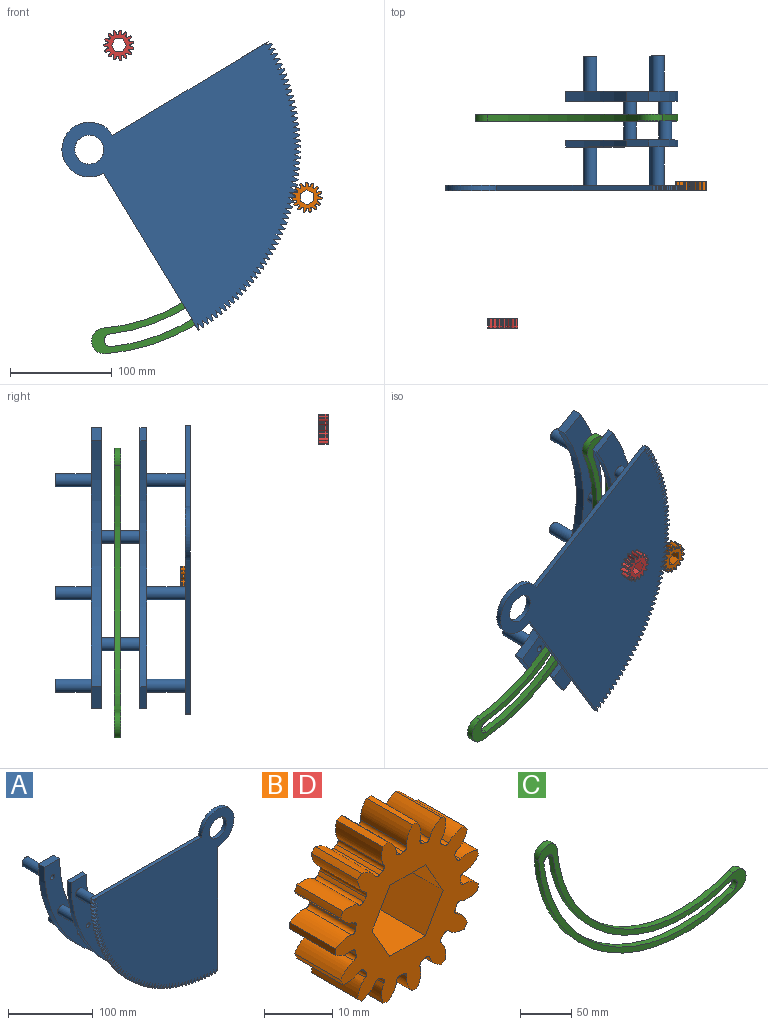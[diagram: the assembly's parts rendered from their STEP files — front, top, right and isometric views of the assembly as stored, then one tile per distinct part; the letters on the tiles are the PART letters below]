
ASSEMBLY  parts=4 mates=2
PART A: 217 faces, bbox 234.6x132.6x234.5 mm
  f0: extruded ~5.08x4.11mm, area 22mm2, adj f1,f2,f178,f180
  f1: plane 234.57x234.55mm, normal (0,-1,0), area 34241.1mm2, adj f0,f3,f4,f5,f6,f7,f8,f9
  f2: plane 234.57x234.55mm, normal (0,1,0), area 33861.1mm2, adj f0,f3,f4,f5,f6,f7,f8,f9
  f3: cylinder r=207.58mm len=5.08mm, axis (0,1,0), area 3.6mm2, adj f1,f2,f4,f179
  f4: extruded ~5.89x5.08mm, area 31.6mm2, adj f1,f2,f3,f5
  f5: extruded ~5.83x5.08mm, area 31.6mm2, adj f1,f2,f4,f6
  f6: cylinder r=207.58mm len=5.08mm, axis (0,1,0), area 7.3mm2, adj f1,f2,f5,f7
  f7: extruded ~5.94x5.08mm, area 31.6mm2, adj f1,f2,f6,f8
  f8: extruded ~5.77x5.08mm, area 31.6mm2, adj f1,f2,f7,f9
  f9: cylinder r=207.58mm len=5.08mm, axis (0,1,0), area 7.3mm2, adj f1,f2,f8,f10
  f10: extruded ~5.98x5.08mm, area 31.6mm2, adj f1,f2,f9,f11
  f11: extruded ~5.71x5.08mm, area 31.6mm2, adj f1,f2,f10,f12
  f12: cylinder r=207.58mm len=5.08mm, axis (0,1,0), area 7.3mm2, adj f1,f2,f11,f13
  f13: extruded ~6.02x5.08mm, area 31.6mm2, adj f1,f2,f12,f14
  f14: extruded ~5.64x5.08mm, area 31.6mm2, adj f1,f2,f13,f15
  f15: cylinder r=207.58mm len=5.08mm, axis (0,1,0), area 7.3mm2, adj f1,f2,f14,f16
  f16: extruded ~6.06x5.08mm, area 31.6mm2, adj f1,f2,f15,f17
  f17: extruded ~5.57x5.08mm, area 31.6mm2, adj f1,f2,f16,f18
  f18: cylinder r=207.58mm len=5.08mm, axis (0,1,0), area 7.3mm2, adj f1,f2,f17,f19
  f19: extruded ~6.1x5.08mm, area 31.6mm2, adj f1,f2,f18,f20
  f20: extruded ~5.49x5.08mm, area 31.6mm2, adj f1,f2,f19,f21
  f21: cylinder r=207.58mm len=5.08mm, axis (0,1,0), area 7.3mm2, adj f1,f2,f20,f22
  f22: extruded ~6.13x5.08mm, area 31.6mm2, adj f1,f2,f21,f23
  f23: extruded ~5.41x5.08mm, area 31.6mm2, adj f1,f2,f22,f24
  f24: cylinder r=207.58mm len=5.08mm, axis (0,1,0), area 7.3mm2, adj f1,f2,f23,f25
  f25: extruded ~6.15x5.08mm, area 31.6mm2, adj f1,f2,f24,f26
  f26: extruded ~5.33x5.08mm, area 31.6mm2, adj f1,f2,f25,f27
  f27: cylinder r=207.58mm len=5.08mm, axis (0,1,0), area 7.3mm2, adj f1,f2,f26,f28
  f28: extruded ~6.17x5.08mm, area 31.6mm2, adj f1,f2,f27,f29
  f29: extruded ~5.24x5.08mm, area 31.6mm2, adj f1,f2,f28,f30
  f30: cylinder r=207.58mm len=5.08mm, axis (0,1,0), area 7.3mm2, adj f1,f2,f29,f31
  f31: extruded ~6.19x5.08mm, area 31.6mm2, adj f1,f2,f30,f32
  f32: extruded ~5.15x5.08mm, area 31.6mm2, adj f1,f2,f31,f33
  f33: cylinder r=207.58mm len=5.08mm, axis (0,1,0), area 7.3mm2, adj f1,f2,f32,f34
  f34: extruded ~6.2x5.08mm, area 31.6mm2, adj f1,f2,f33,f35
  f35: extruded ~5.08x5.06mm, area 31.6mm2, adj f1,f2,f34,f36
  f36: cylinder r=207.58mm len=5.08mm, axis (0,1,0), area 7.3mm2, adj f1,f2,f35,f37
  f37: extruded ~6.21x5.08mm, area 31.6mm2, adj f1,f2,f36,f38
  f38: extruded ~5.08x4.96mm, area 31.6mm2, adj f1,f2,f37,f39
  f39: cylinder r=207.58mm len=5.08mm, axis (0,1,0), area 7.3mm2, adj f1,f2,f38,f40
  f40: extruded ~6.21x5.08mm, area 31.6mm2, adj f1,f2,f39,f41
  f41: extruded ~5.08x4.86mm, area 31.6mm2, adj f1,f2,f40,f42
  f42: cylinder r=207.58mm len=5.08mm, axis (0,1,0), area 7.3mm2, adj f1,f2,f41,f43
  f43: extruded ~6.21x5.08mm, area 31.6mm2, adj f1,f2,f42,f44
  f44: extruded ~5.08x4.75mm, area 31.6mm2, adj f1,f2,f43,f45
  f45: cylinder r=207.58mm len=5.08mm, axis (0,1,0), area 7.3mm2, adj f1,f2,f44,f46
  f46: extruded ~6.2x5.08mm, area 31.6mm2, adj f1,f2,f45,f47
  f47: extruded ~5.08x4.65mm, area 31.6mm2, adj f1,f2,f46,f48
  f48: cylinder r=207.58mm len=5.08mm, axis (0,1,0), area 7.3mm2, adj f1,f2,f47,f49
  f49: extruded ~6.19x5.08mm, area 31.6mm2, adj f1,f2,f48,f50
  f50: extruded ~5.08x4.53mm, area 31.6mm2, adj f1,f2,f49,f51
  f51: cylinder r=207.58mm len=5.08mm, axis (0,1,0), area 7.3mm2, adj f1,f2,f50,f52
  f52: extruded ~6.18x5.08mm, area 31.6mm2, adj f1,f2,f51,f53
  f53: extruded ~5.08x4.42mm, area 31.6mm2, adj f1,f2,f52,f54
  f54: cylinder r=207.58mm len=5.08mm, axis (0,1,0), area 7.3mm2, adj f1,f2,f53,f55
  f55: extruded ~6.16x5.08mm, area 31.6mm2, adj f1,f2,f54,f56
  f56: extruded ~5.08x4.48mm, area 31.6mm2, adj f1,f2,f55,f57
  f57: cylinder r=207.58mm len=5.08mm, axis (0,1,0), area 7.3mm2, adj f1,f2,f56,f58
  f58: extruded ~6.13x5.08mm, area 31.6mm2, adj f1,f2,f57,f59
  f59: extruded ~5.08x4.59mm, area 31.6mm2, adj f1,f2,f58,f60
  f60: cylinder r=207.58mm len=5.08mm, axis (0,1,0), area 7.3mm2, adj f1,f2,f59,f61
  f61: extruded ~6.11x5.08mm, area 31.6mm2, adj f1,f2,f60,f62
  f62: extruded ~5.08x4.7mm, area 31.6mm2, adj f1,f2,f61,f63
  f63: cylinder r=207.58mm len=5.08mm, axis (0,1,0), area 7.3mm2, adj f1,f2,f62,f64
  f64: extruded ~6.07x5.08mm, area 31.6mm2, adj f1,f2,f63,f65
  f65: extruded ~5.08x4.81mm, area 31.6mm2, adj f1,f2,f64,f66
  f66: cylinder r=207.58mm len=5.08mm, axis (0,1,0), area 7.3mm2, adj f1,f2,f65,f67
  f67: extruded ~6.04x5.08mm, area 31.6mm2, adj f1,f2,f66,f68
  f68: extruded ~5.08x4.91mm, area 31.6mm2, adj f1,f2,f67,f69
  f69: cylinder r=207.58mm len=5.08mm, axis (0,1,0), area 7.3mm2, adj f1,f2,f68,f70
  f70: extruded ~5.99x5.08mm, area 31.6mm2, adj f1,f2,f69,f71
  f71: extruded ~5.08x5.01mm, area 31.6mm2, adj f1,f2,f70,f72
  f72: cylinder r=207.58mm len=5.08mm, axis (0,1,0), area 7.3mm2, adj f1,f2,f71,f73
  f73: extruded ~5.95x5.08mm, area 31.6mm2, adj f1,f2,f72,f74
  f74: extruded ~5.11x5.08mm, area 31.6mm2, adj f1,f2,f73,f75
  f75: cylinder r=207.58mm len=5.08mm, axis (0,1,0), area 7.3mm2, adj f1,f2,f74,f76
  f76: extruded ~5.9x5.08mm, area 31.6mm2, adj f1,f2,f75,f77
  f77: extruded ~5.2x5.08mm, area 31.6mm2, adj f1,f2,f76,f78
  f78: cylinder r=207.58mm len=5.08mm, axis (0,1,0), area 7.3mm2, adj f1,f2,f77,f79
  f79: extruded ~5.85x5.08mm, area 31.6mm2, adj f1,f2,f78,f80
  f80: extruded ~5.29x5.08mm, area 31.6mm2, adj f1,f2,f79,f81
  f81: cylinder r=207.58mm len=5.08mm, axis (0,1,0), area 7.3mm2, adj f1,f2,f80,f82
  f82: extruded ~5.79x5.08mm, area 31.6mm2, adj f1,f2,f81,f83
  f83: extruded ~5.38x5.08mm, area 31.6mm2, adj f1,f2,f82,f84
  f84: cylinder r=207.58mm len=5.08mm, axis (0,1,0), area 7.3mm2, adj f1,f2,f83,f85
  f85: extruded ~5.73x5.08mm, area 31.6mm2, adj f1,f2,f84,f86
  f86: extruded ~5.46x5.08mm, area 31.6mm2, adj f1,f2,f85,f87
  f87: cylinder r=207.58mm len=5.08mm, axis (0,1,0), area 7.3mm2, adj f1,f2,f86,f88
  f88: extruded ~5.66x5.08mm, area 31.6mm2, adj f1,f2,f87,f89
  f89: extruded ~5.53x5.08mm, area 31.6mm2, adj f1,f2,f88,f90
  f90: cylinder r=207.58mm len=5.08mm, axis (0,1,0), area 7.3mm2, adj f1,f2,f89,f91
  f91: extruded ~5.59x5.08mm, area 31.6mm2, adj f1,f2,f90,f92
  f92: extruded ~5.61x5.08mm, area 31.6mm2, adj f1,f2,f91,f93
  f93: cylinder r=207.58mm len=5.08mm, axis (0,1,0), area 7.3mm2, adj f1,f2,f92,f94
  f94: extruded ~5.51x5.08mm, area 31.6mm2, adj f1,f2,f93,f95
  f95: extruded ~5.68x5.08mm, area 31.6mm2, adj f1,f2,f94,f96
  f96: cylinder r=207.58mm len=5.08mm, axis (0,1,0), area 7.3mm2, adj f1,f2,f95,f97
  f97: extruded ~5.44x5.08mm, area 31.6mm2, adj f1,f2,f96,f98
  f98: extruded ~5.74x5.08mm, area 31.6mm2, adj f1,f2,f97,f99
  f99: cylinder r=207.58mm len=5.08mm, axis (0,1,0), area 7.3mm2, adj f1,f2,f98,f100
  f100: extruded ~5.35x5.08mm, area 31.6mm2, adj f1,f2,f99,f101
  f101: extruded ~5.8x5.08mm, area 31.6mm2, adj f1,f2,f100,f102
  f102: cylinder r=207.58mm len=5.08mm, axis (0,1,0), area 7.3mm2, adj f1,f2,f101,f103
  f103: extruded ~5.27x5.08mm, area 31.6mm2, adj f1,f2,f102,f104
  f104: extruded ~5.86x5.08mm, area 31.6mm2, adj f1,f2,f103,f105
  f105: cylinder r=207.58mm len=5.08mm, axis (0,1,0), area 7.3mm2, adj f1,f2,f104,f106
  f106: extruded ~5.18x5.08mm, area 31.6mm2, adj f1,f2,f105,f107
  f107: extruded ~5.91x5.08mm, area 31.6mm2, adj f1,f2,f106,f108
  f108: cylinder r=207.58mm len=5.08mm, axis (0,1,0), area 7.3mm2, adj f1,f2,f107,f109
  f109: extruded ~5.09x5.08mm, area 31.6mm2, adj f1,f2,f108,f110
  f110: extruded ~5.96x5.08mm, area 31.6mm2, adj f1,f2,f109,f111
  f111: cylinder r=207.58mm len=5.08mm, axis (0,1,0), area 7.3mm2, adj f1,f2,f110,f112
  f112: extruded ~5.08x4.99mm, area 31.6mm2, adj f1,f2,f111,f113
  f113: extruded ~6.01x5.08mm, area 31.6mm2, adj f1,f2,f112,f114
  f114: cylinder r=207.58mm len=5.08mm, axis (0,1,0), area 7.3mm2, adj f1,f2,f113,f115
  f115: extruded ~5.08x4.89mm, area 31.6mm2, adj f1,f2,f114,f116
  f116: extruded ~6.05x5.08mm, area 31.6mm2, adj f1,f2,f115,f117
  f117: cylinder r=207.58mm len=5.08mm, axis (0,1,0), area 7.3mm2, adj f1,f2,f116,f118
  f118: extruded ~5.08x4.78mm, area 31.6mm2, adj f1,f2,f117,f119
  f119: extruded ~6.08x5.08mm, area 31.6mm2, adj f1,f2,f118,f120
  f120: cylinder r=207.58mm len=5.08mm, axis (0,1,0), area 7.3mm2, adj f1,f2,f119,f121
  f121: extruded ~5.08x4.68mm, area 31.6mm2, adj f1,f2,f120,f122
  f122: extruded ~6.11x5.08mm, area 31.6mm2, adj f1,f2,f121,f123
  f123: cylinder r=207.58mm len=5.08mm, axis (0,1,0), area 7.3mm2, adj f1,f2,f122,f124
  f124: extruded ~5.08x4.56mm, area 31.6mm2, adj f1,f2,f123,f125
  f125: extruded ~6.14x5.08mm, area 31.6mm2, adj f1,f2,f124,f126
  f126: cylinder r=207.58mm len=5.08mm, axis (0,1,0), area 7.3mm2, adj f1,f2,f125,f127
  f127: extruded ~5.08x4.45mm, area 31.6mm2, adj f1,f2,f126,f128
  f128: extruded ~6.16x5.08mm, area 31.6mm2, adj f1,f2,f127,f129
  f129: cylinder r=207.58mm len=5.08mm, axis (0,1,0), area 7.3mm2, adj f1,f2,f128,f130
  f130: extruded ~5.08x4.45mm, area 31.6mm2, adj f1,f2,f129,f131
  f131: extruded ~6.18x5.08mm, area 31.6mm2, adj f1,f2,f130,f132
  f132: cylinder r=207.58mm len=5.08mm, axis (0,1,0), area 7.3mm2, adj f1,f2,f131,f133
  f133: extruded ~5.08x4.56mm, area 31.6mm2, adj f1,f2,f132,f134
  f134: extruded ~6.19x5.08mm, area 31.6mm2, adj f1,f2,f133,f135
  f135: cylinder r=207.58mm len=5.08mm, axis (0,1,0), area 7.3mm2, adj f1,f2,f134,f136
  f136: extruded ~5.08x4.67mm, area 31.6mm2, adj f1,f2,f135,f137
  f137: extruded ~6.2x5.08mm, area 31.6mm2, adj f1,f2,f136,f138
  f138: cylinder r=207.58mm len=5.08mm, axis (0,1,0), area 7.3mm2, adj f1,f2,f137,f139
  f139: extruded ~5.08x4.78mm, area 31.6mm2, adj f1,f2,f138,f140
  f140: extruded ~6.21x5.08mm, area 31.6mm2, adj f1,f2,f139,f141
  f141: cylinder r=207.58mm len=5.08mm, axis (0,1,0), area 7.3mm2, adj f1,f2,f140,f142
  f142: extruded ~5.08x4.88mm, area 31.6mm2, adj f1,f2,f141,f143
  f143: extruded ~6.21x5.08mm, area 31.6mm2, adj f1,f2,f142,f144
  f144: cylinder r=207.58mm len=5.08mm, axis (0,1,0), area 7.3mm2, adj f1,f2,f143,f145
  f145: extruded ~5.08x4.99mm, area 31.6mm2, adj f1,f2,f144,f146
  f146: extruded ~6.21x5.08mm, area 31.6mm2, adj f1,f2,f145,f147
  f147: cylinder r=207.58mm len=5.08mm, axis (0,1,0), area 7.3mm2, adj f1,f2,f146,f148
  f148: extruded ~5.08x5.08mm, area 31.6mm2, adj f1,f2,f147,f149
  f149: extruded ~6.2x5.08mm, area 31.6mm2, adj f1,f2,f148,f150
  f150: cylinder r=207.58mm len=5.08mm, axis (0,1,0), area 7.3mm2, adj f1,f2,f149,f151
  f151: extruded ~5.18x5.08mm, area 31.6mm2, adj f1,f2,f150,f152
  f152: extruded ~6.18x5.08mm, area 31.6mm2, adj f1,f2,f151,f153
  f153: cylinder r=207.58mm len=5.08mm, axis (0,1,0), area 7.3mm2, adj f1,f2,f152,f154
  f154: extruded ~5.27x5.08mm, area 31.6mm2, adj f1,f2,f153,f155
  f155: extruded ~6.17x5.08mm, area 31.6mm2, adj f1,f2,f154,f156
  f156: cylinder r=207.58mm len=5.08mm, axis (0,1,0), area 7.3mm2, adj f1,f2,f155,f157
  f157: extruded ~5.35x5.08mm, area 31.6mm2, adj f1,f2,f156,f158
  f158: extruded ~6.14x5.08mm, area 31.6mm2, adj f1,f2,f157,f159
  f159: cylinder r=207.58mm len=5.08mm, axis (0,1,0), area 7.3mm2, adj f1,f2,f158,f160
  f160: extruded ~5.43x5.08mm, area 31.6mm2, adj f1,f2,f159,f161
  f161: extruded ~6.12x5.08mm, area 31.6mm2, adj f1,f2,f160,f162
  f162: cylinder r=207.58mm len=5.08mm, axis (0,1,0), area 7.3mm2, adj f1,f2,f161,f163
  f163: extruded ~5.51x5.08mm, area 31.6mm2, adj f1,f2,f162,f164
  f164: extruded ~6.09x5.08mm, area 31.6mm2, adj f1,f2,f163,f165
  f165: cylinder r=207.58mm len=5.08mm, axis (0,1,0), area 7.3mm2, adj f1,f2,f164,f166
  f166: extruded ~5.59x5.08mm, area 31.6mm2, adj f1,f2,f165,f167
  f167: extruded ~6.05x5.08mm, area 31.6mm2, adj f1,f2,f166,f168
  f168: cylinder r=207.58mm len=5.08mm, axis (0,1,0), area 7.3mm2, adj f1,f2,f167,f169
  f169: extruded ~5.66x5.08mm, area 31.6mm2, adj f1,f2,f168,f170
  f170: extruded ~6.01x5.08mm, area 31.6mm2, adj f1,f2,f169,f171
  f171: cylinder r=207.58mm len=5.08mm, axis (0,1,0), area 7.3mm2, adj f1,f2,f170,f172
  f172: extruded ~5.72x5.08mm, area 31.6mm2, adj f1,f2,f171,f173
  f173: extruded ~5.97x5.08mm, area 31.6mm2, adj f1,f2,f172,f174
  f174: cylinder r=207.58mm len=5.08mm, axis (0,1,0), area 7.3mm2, adj f1,f2,f173,f175
  f175: extruded ~5.79x5.08mm, area 31.6mm2, adj f1,f2,f174,f176
  f176: extruded ~5.92x5.08mm, area 31.6mm2, adj f1,f2,f175,f177
  f177: cylinder r=207.58mm len=5.08mm, axis (0,1,0), area 7.3mm2, adj f1,f2,f176,f178
  f178: extruded ~5.84x5.08mm, area 31.6mm2, adj f0,f1,f2,f177
  f179: plane 180.59x5.08mm, normal (0,0,1), area 917.4mm2, adj f1,f2,f3,f181
  f180: plane 178.83x5.08mm, normal (1,0,0), area 908.4mm2, adj f0,f1,f2,f181
  f181: cylinder r=26.99mm len=53.98mm, axis (0,1,0), area 646.1mm2, adj f1,f2,f179,f180
  f182: cylinder r=14.29mm len=28.58mm, axis (0,1,0), area 456mm2, adj f1,f2
  f183: cylinder r=6.35mm len=38.1mm, axis (0,-1,0), area 1520.1mm2, adj f2,f193
  f184: cylinder r=6.35mm len=38.1mm, axis (0,-1,0), area 1520.1mm2, adj f2,f193
  f185: cylinder r=6.35mm len=38.1mm, axis (0,-1,0), area 1520.1mm2, adj f2,f193
  f186: plane 25.4x6.6mm, normal (1,0,0), area 167.7mm2, adj f187,f190,f192,f193
  f187: cylinder r=201.61mm len=201.61mm, axis (0,-1,0), area 2091.4mm2, adj f186,f188,f192,f193
  f188: plane 25.4x6.6mm, normal (0,0,1), area 167.7mm2, adj f187,f190,f192,f193
  f189: cylinder r=3.17mm len=54.61mm, axis (0,-1,0), area 1089.4mm2, adj f193,f216
  f190: cylinder r=176.21mm len=176.21mm, axis (0,-1,0), area 1827.9mm2, adj f186,f188,f192,f193
  f191: cylinder r=3.17mm len=54.61mm, axis (0,-1,0), area 1089.4mm2, adj f193,f216
  f192: plane 201.61x201.61mm, normal (0,1,0), area 7188.9mm2, adj f186,f187,f188,f190,f195,f197,f199,f200
  f193: plane 201.61x201.61mm, normal (0,-1,0), area 7093.9mm2, adj f183,f184,f185,f186,f187,f188,f189,f190
  f194: plane 6.35x6.35mm, normal (0,1,0), area 31.7mm2, adj f195
  f195: cylinder r=3.17mm len=44.7mm, axis (0,-1,0), area 891.8mm2, adj f192,f194
  f196: plane 6.35x6.35mm, normal (0,1,0), area 31.7mm2, adj f197
  f197: cylinder r=3.17mm len=44.7mm, axis (0,-1,0), area 891.8mm2, adj f192,f196
  f198: plane 6.35x6.35mm, normal (0,1,0), area 31.7mm2, adj f199
  f199: cylinder r=3.17mm len=44.7mm, axis (0,-1,0), area 891.8mm2, adj f192,f198
  f200: cylinder r=6.35mm len=38.1mm, axis (0,-1,0), area 1520.1mm2, adj f192,f209
  f201: cylinder r=6.35mm len=38.1mm, axis (0,-1,0), area 1520.1mm2, adj f192,f209
  f202: plane 25.4x9.91mm, normal (0,0,1), area 251.6mm2, adj f203,f205,f209,f216
  f203: cylinder r=176.21mm len=176.21mm, axis (0,-1,0), area 2741.9mm2, adj f202,f204,f209,f216
  f204: plane 25.4x9.91mm, normal (1,0,0), area 251.6mm2, adj f203,f205,f209,f216
  f205: cylinder r=201.61mm len=201.61mm, axis (0,-1,0), area 3137.2mm2, adj f202,f204,f209,f216
  f206: cylinder r=3.17mm len=44.7mm, axis (0,-1,0), area 891.8mm2, adj f209,f215
  f207: cylinder r=3.17mm len=44.7mm, axis (0,-1,0), area 891.8mm2, adj f209,f213
  f208: cylinder r=3.17mm len=44.7mm, axis (0,-1,0), area 891.8mm2, adj f209,f211
  f209: plane 201.61x201.61mm, normal (0,-1,0), area 7188.9mm2, adj f200,f201,f202,f203,f204,f205,f206,f207
  f210: cylinder r=6.35mm len=34.8mm, axis (0,-1,0), area 1388.4mm2, adj f211,f216
  f211: plane 12.7x12.7mm, normal (0,1,0), area 95mm2, adj f208,f210
  f212: cylinder r=6.35mm len=34.8mm, axis (0,-1,0), area 1388.4mm2, adj f213,f216
  f213: plane 12.7x12.7mm, normal (0,1,0), area 95mm2, adj f207,f212
  f214: cylinder r=6.35mm len=34.8mm, axis (0,-1,0), area 1388.4mm2, adj f215,f216
  f215: plane 12.7x12.7mm, normal (0,1,0), area 95mm2, adj f206,f214
  f216: plane 201.61x201.61mm, normal (0,1,0), area 7093.9mm2, adj f189,f191,f202,f203,f204,f205,f210,f212
PART B: 98 faces, bbox 29.6x9.5x29.8 mm
  f0: plane 29.76x29.6mm, normal (0,-1,0), area 386.4mm2, adj f2,f3,f4,f5,f6,f7,f8,f9
  f1: plane 29.76x29.6mm, normal (0,1,0), area 386.4mm2, adj f2,f3,f4,f5,f6,f7,f8,f9
  f2: extruded ~9.53x3.13mm, area 34mm2, adj f0,f1,f61,f62
  f3: cylinder r=10.95mm len=9.53mm, axis (0,1,0), area 6.9mm2, adj f0,f1,f62,f63
  f4: extruded ~9.53x3.13mm, area 34mm2, adj f0,f1,f5,f63
  f5: cylinder r=14.89mm len=9.53mm, axis (0,1,0), area 10.9mm2, adj f0,f1,f4,f6
  f6: extruded ~9.53x3.47mm, area 34mm2, adj f0,f1,f5,f64
  f7: cylinder r=10.95mm len=9.53mm, axis (0,1,0), area 6.9mm2, adj f0,f1,f64,f65
  f8: extruded ~9.53x2.64mm, area 34mm2, adj f0,f1,f9,f65
  f9: cylinder r=14.89mm len=9.53mm, axis (0,1,0), area 10.9mm2, adj f0,f1,f8,f10
  f10: extruded ~9.53x3.21mm, area 34mm2, adj f0,f1,f9,f66
  f11: cylinder r=10.95mm len=9.53mm, axis (0,1,0), area 6.9mm2, adj f0,f1,f66,f67
  f12: extruded ~9.53x3.33mm, area 34mm2, adj f0,f1,f13,f67
  f13: cylinder r=14.89mm len=9.53mm, axis (0,1,0), area 10.9mm2, adj f0,f1,f12,f14
  f14: extruded ~9.53x2.52mm, area 34mm2, adj f0,f1,f13,f68
  f15: cylinder r=10.95mm len=9.53mm, axis (0,1,0), area 6.9mm2, adj f0,f1,f68,f69
  f16: extruded ~9.53x3.44mm, area 34mm2, adj f0,f1,f17,f69
  f17: cylinder r=14.89mm len=9.53mm, axis (0,1,0), area 10.9mm2, adj f0,f1,f16,f18
  f18: extruded ~9.53x3.27mm, area 34mm2, adj f0,f1,f17,f70
  f19: cylinder r=10.95mm len=9.53mm, axis (0,1,0), area 6.9mm2, adj f0,f1,f70,f71
  f20: extruded ~9.53x2.96mm, area 34mm2, adj f0,f1,f21,f71
  f21: cylinder r=14.89mm len=9.53mm, axis (0,1,0), area 10.9mm2, adj f0,f1,f20,f22
  f22: extruded ~9.53x3.46mm, area 34mm2, adj f0,f1,f21,f72
  f23: cylinder r=10.95mm len=9.53mm, axis (0,1,0), area 6.9mm2, adj f0,f1,f72,f73
  f24: extruded ~9.53x2.86mm, area 34mm2, adj f0,f1,f25,f73
  f25: cylinder r=14.89mm len=9.53mm, axis (0,1,0), area 10.9mm2, adj f0,f1,f24,f26
  f26: extruded ~9.53x3.05mm, area 34mm2, adj f0,f1,f25,f74
  f27: cylinder r=10.95mm len=9.53mm, axis (0,1,0), area 6.9mm2, adj f0,f1,f74,f75
  f28: extruded ~9.53x3.41mm, area 34mm2, adj f0,f1,f29,f75
  f29: cylinder r=14.89mm len=9.53mm, axis (0,1,0), area 10.9mm2, adj f0,f1,f28,f30
  f30: extruded ~9.53x2.75mm, area 34mm2, adj f0,f1,f29,f76
  f31: cylinder r=10.95mm len=9.53mm, axis (0,1,0), area 6.9mm2, adj f0,f1,f76,f77
  f32: extruded ~9.53x3.38mm, area 34mm2, adj f0,f1,f33,f77
  f33: cylinder r=14.89mm len=9.53mm, axis (0,1,0), area 10.9mm2, adj f0,f1,f32,f34
  f34: extruded ~9.53x3.38mm, area 34mm2, adj f0,f1,f33,f78
  f35: cylinder r=10.95mm len=9.53mm, axis (0,1,0), area 6.9mm2, adj f0,f1,f78,f79
  f36: extruded ~9.53x2.75mm, area 34mm2, adj f0,f1,f37,f79
  f37: cylinder r=14.89mm len=9.53mm, axis (0,1,0), area 10.9mm2, adj f0,f1,f36,f38
  f38: extruded ~9.53x3.41mm, area 34mm2, adj f0,f1,f37,f80
  f39: cylinder r=10.95mm len=9.53mm, axis (0,1,0), area 6.9mm2, adj f0,f1,f80,f81
  f40: extruded ~9.53x3.05mm, area 34mm2, adj f0,f1,f41,f81
  f41: cylinder r=14.89mm len=9.53mm, axis (0,1,0), area 10.9mm2, adj f0,f1,f40,f42
  f42: extruded ~9.53x2.86mm, area 34mm2, adj f0,f1,f41,f82
  f43: cylinder r=10.95mm len=9.53mm, axis (0,1,0), area 6.9mm2, adj f0,f1,f82,f83
  f44: extruded ~9.53x3.46mm, area 34mm2, adj f0,f1,f45,f83
  f45: cylinder r=14.89mm len=9.53mm, axis (0,1,0), area 10.9mm2, adj f0,f1,f44,f46
  f46: extruded ~9.53x2.96mm, area 34mm2, adj f0,f1,f45,f84
  f47: cylinder r=10.95mm len=9.53mm, axis (0,1,0), area 6.9mm2, adj f0,f1,f84,f85
  f48: extruded ~9.53x3.27mm, area 34mm2, adj f0,f1,f49,f85
  f49: cylinder r=14.89mm len=9.53mm, axis (0,1,0), area 10.9mm2, adj f0,f1,f48,f50
  f50: extruded ~9.53x3.44mm, area 34mm2, adj f0,f1,f49,f86
  f51: cylinder r=10.95mm len=9.53mm, axis (0,1,0), area 6.9mm2, adj f0,f1,f86,f87
  f52: extruded ~9.53x2.52mm, area 34mm2, adj f0,f1,f53,f87
  f53: cylinder r=14.89mm len=9.53mm, axis (0,1,0), area 10.9mm2, adj f0,f1,f52,f54
  f54: extruded ~9.53x3.33mm, area 34mm2, adj f0,f1,f53,f88
  f55: cylinder r=10.95mm len=9.53mm, axis (0,1,0), area 6.9mm2, adj f0,f1,f88,f89
  f56: extruded ~9.53x3.21mm, area 34mm2, adj f0,f1,f57,f89
  f57: cylinder r=14.89mm len=9.53mm, axis (0,1,0), area 10.9mm2, adj f0,f1,f56,f58
  f58: extruded ~9.53x2.64mm, area 34mm2, adj f0,f1,f57,f90
  f59: cylinder r=10.95mm len=9.53mm, axis (0,1,0), area 6.9mm2, adj f0,f1,f90,f91
  f60: extruded ~9.53x3.47mm, area 34mm2, adj f0,f1,f61,f91
  f61: cylinder r=14.89mm len=9.53mm, axis (0,1,0), area 10.9mm2, adj f0,f1,f2,f60
  f62: cylinder r=0.65mm len=9.53mm, axis (0,1,0), area 9.5mm2, adj f0,f1,f2,f3
  f63: cylinder r=0.65mm len=9.53mm, axis (0,1,0), area 9.5mm2, adj f0,f1,f3,f4
  f64: cylinder r=0.65mm len=9.53mm, axis (0,1,0), area 9.5mm2, adj f0,f1,f6,f7
  f65: cylinder r=0.65mm len=9.53mm, axis (0,1,0), area 9.5mm2, adj f0,f1,f7,f8
  f66: cylinder r=0.65mm len=9.53mm, axis (0,1,0), area 9.5mm2, adj f0,f1,f10,f11
  f67: cylinder r=0.65mm len=9.53mm, axis (0,1,0), area 9.5mm2, adj f0,f1,f11,f12
  f68: cylinder r=0.65mm len=9.53mm, axis (0,1,0), area 9.5mm2, adj f0,f1,f14,f15
  f69: cylinder r=0.65mm len=9.53mm, axis (0,1,0), area 9.5mm2, adj f0,f1,f15,f16
  f70: cylinder r=0.65mm len=9.53mm, axis (0,1,0), area 9.5mm2, adj f0,f1,f18,f19
  f71: cylinder r=0.65mm len=9.53mm, axis (0,1,0), area 9.5mm2, adj f0,f1,f19,f20
  f72: cylinder r=0.65mm len=9.53mm, axis (0,1,0), area 9.5mm2, adj f0,f1,f22,f23
  f73: cylinder r=0.65mm len=9.53mm, axis (0,1,0), area 9.5mm2, adj f0,f1,f23,f24
  f74: cylinder r=0.65mm len=9.53mm, axis (0,1,0), area 9.5mm2, adj f0,f1,f26,f27
  f75: cylinder r=0.65mm len=9.53mm, axis (0,1,0), area 9.5mm2, adj f0,f1,f27,f28
  f76: cylinder r=0.65mm len=9.53mm, axis (0,1,0), area 9.5mm2, adj f0,f1,f30,f31
  f77: cylinder r=0.65mm len=9.53mm, axis (0,1,0), area 9.5mm2, adj f0,f1,f31,f32
  f78: cylinder r=0.65mm len=9.53mm, axis (0,1,0), area 9.5mm2, adj f0,f1,f34,f35
  f79: cylinder r=0.65mm len=9.53mm, axis (0,1,0), area 9.5mm2, adj f0,f1,f35,f36
  f80: cylinder r=0.65mm len=9.53mm, axis (0,1,0), area 9.5mm2, adj f0,f1,f38,f39
  f81: cylinder r=0.65mm len=9.53mm, axis (0,1,0), area 9.5mm2, adj f0,f1,f39,f40
  f82: cylinder r=0.65mm len=9.53mm, axis (0,1,0), area 9.5mm2, adj f0,f1,f42,f43
  f83: cylinder r=0.65mm len=9.53mm, axis (0,1,0), area 9.5mm2, adj f0,f1,f43,f44
  f84: cylinder r=0.65mm len=9.53mm, axis (0,1,0), area 9.5mm2, adj f0,f1,f46,f47
  f85: cylinder r=0.65mm len=9.53mm, axis (0,1,0), area 9.5mm2, adj f0,f1,f47,f48
  f86: cylinder r=0.65mm len=9.53mm, axis (0,1,0), area 9.5mm2, adj f0,f1,f50,f51
  f87: cylinder r=0.65mm len=9.53mm, axis (0,1,0), area 9.5mm2, adj f0,f1,f51,f52
  f88: cylinder r=0.65mm len=9.53mm, axis (0,1,0), area 9.5mm2, adj f0,f1,f54,f55
  f89: cylinder r=0.65mm len=9.53mm, axis (0,1,0), area 9.5mm2, adj f0,f1,f55,f56
  f90: cylinder r=0.65mm len=9.53mm, axis (0,1,0), area 9.5mm2, adj f0,f1,f58,f59
  f91: cylinder r=0.65mm len=9.53mm, axis (0,1,0), area 9.5mm2, adj f0,f1,f59,f60
  f92: plane 9.53x6.35mm, normal (0.87,0,-0.5), area 69.8mm2, adj f0,f1,f93,f97
  f93: plane 9.53x6.35mm, normal (0.87,0,0.5), area 69.8mm2, adj f0,f1,f92,f94
  f94: plane 9.53x7.33mm, normal (0,0,1), area 69.8mm2, adj f0,f1,f93,f95
  f95: plane 9.53x6.35mm, normal (-0.87,0,0.5), area 69.8mm2, adj f0,f1,f94,f96
  f96: plane 9.53x6.35mm, normal (-0.87,0,-0.5), area 69.8mm2, adj f0,f1,f95,f97
  f97: plane 9.53x7.33mm, normal (0,0,-1), area 69.8mm2, adj f0,f1,f92,f96
PART C: 10 faces, bbox 285.2x6.6x199.5 mm
  f0: cylinder r=182.56mm len=244.81mm, axis (0,-1,0), area 2186.1mm2, adj f2,f7,f8,f9
  f1: cylinder r=195.26mm len=261.84mm, axis (0,-1,0), area 2338.2mm2, adj f2,f7,f8,f9
  f2: cylinder r=6.35mm len=12.66mm, axis (0,-1,0), area 131.7mm2, adj f0,f1,f8,f9
  f3: cylinder r=12.7mm len=25.36mm, axis (0,-1,0), area 263.5mm2, adj f4,f6,f8,f9
  f4: cylinder r=176.21mm len=242.38mm, axis (0,-1,0), area 2188.3mm2, adj f3,f5,f8,f9
  f5: cylinder r=12.7mm len=24.46mm, axis (0,-1,0), area 263.5mm2, adj f4,f6,f8,f9
  f6: cylinder r=201.61mm len=277.31mm, axis (0,-1,0), area 2503.7mm2, adj f3,f5,f8,f9
  f7: cylinder r=6.35mm len=12.31mm, axis (0,-1,0), area 131.7mm2, adj f0,f1,f8,f9
  f8: plane 285.24x199.48mm, normal (0,1,0), area 5052.9mm2, adj f0,f1,f2,f3,f4,f5,f6,f7
  f9: plane 285.24x199.48mm, normal (0,-1,0), area 5052.9mm2, adj f0,f1,f2,f3,f4,f5,f6,f7
PART D: same geometry as B
PLACE A rot(axis=(0,-1,0),121.2deg) t=(0,-70.1,0)mm
PLACE B rot(axis=(0,-1,0),31.2deg) t=(214.27,-65.66,-46.9)mm
PLACE C rot(axis=(0,-1,0),90deg) t=(0,-67.06,0)mm
PLACE D t=(29.08,-201.21,102.7)mm
MATE fastened B.f0 <-> A.f1  axis (0,-1,0) through (200.2,-75.18,-42.04)mm
MATE revolute C.f0 <-> A.f3  axis (0,-1,0) through (0,-6.6,0)mm
